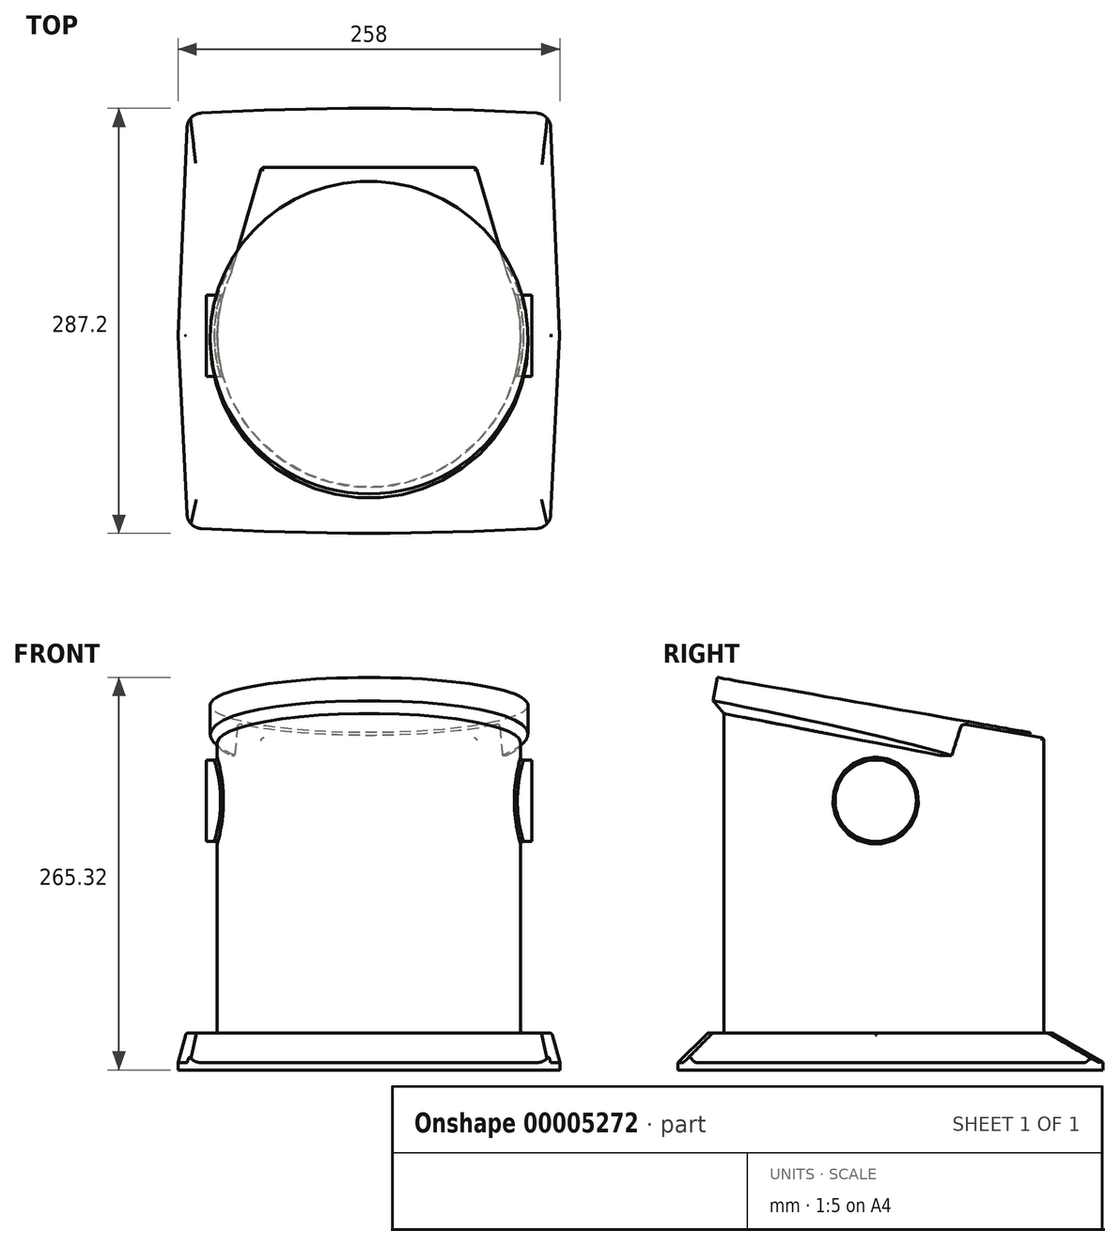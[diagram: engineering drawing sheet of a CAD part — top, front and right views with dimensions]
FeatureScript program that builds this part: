
annotation { "Feature Type Name" : "Feature", "Feature Type Description" : "" }
export const myFeature = defineFeature(function(context is Context, id is Id, definition is map)
    precondition{}
    {
        {
            var Q0;
            Q0=qCreatedBy(makeId("Top.planeOp"),FACE);
            var sketch = newSketch(context, id + "F0", { "sketchPlane" : qUnion([Q0])});
            skLineSegment(sketch, "E0", {"start": v(-129, 0) * mm, "end": v(-122.5, 149.86) * mm});
            skLineSegment(sketch, "E1", {"start": v(-122.5, 149.86) * mm, "end": v(122.5, 149.86) * mm, "construction": true});
            skLineSegment(sketch, "E2", {"start": v(122.5, 149.86) * mm, "end": v(129, 0) * mm});
            skLineSegment(sketch, "E3", {"start": v(129, 0) * mm, "end": v(122.5, -129.84) * mm});
            skLineSegment(sketch, "E4", {"start": v(122.5, -129.84) * mm, "end": v(-122.5, -129.84) * mm, "construction": true});
            skLineSegment(sketch, "E5", {"start": v(-122.5, -129.84) * mm, "end": v(-129, 0) * mm});
            skArc(sketch, "E6", {"start": v(122.5, 149.86) * mm, "mid": v(0, 153.61) * mm, "end": v(-122.5, 149.86) * mm});
            skArc(sketch, "E7", {"start": v(-122.5, -129.84) * mm, "mid": v(0, -133.6) * mm, "end": v(122.5, -129.84) * mm});
            skLineSegment(sketch, "E8", {"start": v(-129, 0) * mm, "end": v(129, 0) * mm, "construction": true});
            skPoint(sketch, "E9", {"position": v(0, 0) * mm});
            skPoint(sketch, "E10", {"position": v(0, 149.86) * mm});
            skPoint(sketch, "E11", {"position": v(0, -129.84) * mm});
            skSolve(sketch);
        }
        {
            var Q0;
            Q0=makeQuery(id+"F0.imprint","IMPRINT",FACE,{"disambiguationData":[TD([[makeQuery(id+"F0.imprint","IMPRINT",EDGE,{"derivedFrom":sQuery(id+"F0.wireOp",EDGE,"E0")}),-1.0]])]});
            extrude(context, id + "F1", {"entities" : qUnion([Q0]), "depth" : 25 * mm});
        }
        {
            var Q0;
            Q0=makeQuery(id+"F1.opExtrude","CAP_EDGE",EDGE,{"disambiguationData":[OSD([sQuery(id+"F0.wireOp",EDGE,"E0")])],"isStart":false});
            var Q1;
            Q1=makeQuery(id+"F1.opExtrude","CAP_EDGE",EDGE,{"disambiguationData":[OSD([sQuery(id+"F0.wireOp",EDGE,"E5")])],"isStart":false});
            var Q2;
            Q2=makeQuery(id+"F1.opExtrude","CAP_EDGE",EDGE,{"disambiguationData":[OSD([sQuery(id+"F0.wireOp",EDGE,"E3")])],"isStart":false});
            var Q3;
            Q3=makeQuery(id+"F1.opExtrude","CAP_EDGE",EDGE,{"disambiguationData":[OSD([sQuery(id+"F0.wireOp",EDGE,"E2")])],"isStart":false});
            chamfer(context, id + "F2", {"entities" : qUnion([Q0, Q1, Q2, Q3]), "chamferType" : ChamferType.OFFSET_ANGLE, "width" : 20 * mm, "oppositeDirection" : false, "angle" : 15 * degree, "tangentPropagation" : true});
        }
        {
            var Q0;
            Q0=makeQuery(id+"F1.opExtrude","CAP_EDGE",EDGE,{"disambiguationData":[OSD([sQuery(id+"F0.wireOp",EDGE,"E7")])],"isStart":false});
            chamfer(context, id + "F3", {"entities" : qUnion([Q0]), "chamferType" : ChamferType.OFFSET_ANGLE, "width" : 20 * mm, "oppositeDirection" : false, "angle" : 45 * degree, "tangentPropagation" : true});
        }
        {
            var Q0;
            Q0=makeQuery(id+"F1.opExtrude","CAP_EDGE",EDGE,{"disambiguationData":[OSD([sQuery(id+"F0.wireOp",EDGE,"E6")])],"isStart":false});
            chamfer(context, id + "F4", {"entities" : qUnion([Q0]), "chamferType" : ChamferType.OFFSET_ANGLE, "width" : 34 * mm, "oppositeDirection" : false, "angle" : 30 * degree, "tangentPropagation" : true});
        }
        {
            var Q0;
            Q0=makeQuery(id+"F1.opExtrude","CAP_FACE",FACE,{"disambiguationData":[OSD([sQuery(id+"F0.wireOp",EDGE,"E0"),sQuery(id+"F0.wireOp",EDGE,"E2"),sQuery(id+"F0.wireOp",EDGE,"E3"),sQuery(id+"F0.wireOp",EDGE,"E5"),sQuery(id+"F0.wireOp",EDGE,"E6"),sQuery(id+"F0.wireOp",EDGE,"E7")])],"isStart":false});
            var sketch = newSketch(context, id + "F5", { "sketchPlane" : qUnion([Q0])});
            skArc(sketch, "E12", {"start": v(-92.81, 43.5) * mm, "mid": v(0, -102.5) * mm, "end": v(92.81, 43.5) * mm});
            skLineSegment(sketch, "E13", {"start": v(-92.81, 43.5) * mm, "end": v(-72.5, 113.61) * mm});
            skLineSegment(sketch, "E14", {"start": v(-72.5, 113.61) * mm, "end": v(72.5, 113.61) * mm});
            skLineSegment(sketch, "E15", {"start": v(72.5, 113.61) * mm, "end": v(92.81, 43.5) * mm});
            skPoint(sketch, "E16", {"position": v(0, 113.61) * mm});
            skSolve(sketch);
        }
        {
            var Q0;
            Q0=makeQuery(id+"F5.imprint","IMPRINT",FACE,{"disambiguationData":[TD([[makeQuery(id+"F5.imprint","IMPRINT",EDGE,{"derivedFrom":sQuery(id+"F5.wireOp",EDGE,"E12")}),1.0]])]});
            extrude(context, id + "F6", {"entities" : qUnion([Q0]), "operationType" : NewBodyOperationType.ADD, "depth" : 240 * mm});
        }
        {
            var Q0;
            Q0=makeQuery(id+"F6.opExtrude","CAP_EDGE",EDGE,{"disambiguationData":[OSD([sQuery(id+"F5.wireOp",EDGE,"E14")])],"isStart":false});
            cPlane(context, id + "F7", {"entities" : qUnion([Q0]), "cplaneType" : CPlaneType.LINE_ANGLE, "offset" : 150 * mm, "angle" : 80 * degree, "width" : 150 * mm, "height" : 150 * mm});
        }
        {
            var Q0;
            Q0=qCreatedBy(id+"F7.planeOp",FACE);
            var sketch = newSketch(context, id + "F8", { "sketchPlane" : qUnion([Q0])});
            skCircle(sketch, "E17", {"center": v(0, -11.31) * mm, "radius": 170.12 * mm});
            skSolve(sketch);
        }
        {
            var Q0;
            Q0=makeQuery(id+"F8.imprint","IMPRINT",FACE,{"disambiguationData":[TD([[makeQuery(id+"F8.imprint","IMPRINT",EDGE,{"derivedFrom":sQuery(id+"F8.wireOp",EDGE,"E17")}),1.0]])]});
            extrude(context, id + "F9", {"entities" : qUnion([Q0]), "operationType" : NewBodyOperationType.REMOVE, "oppositeDirection" : true, "depth" : 40 * mm});
        }
        {
            var Q0;
            Q0=makeQuery(id+"F9.boolean.opBoolean","COPY",FACE,{"derivedFrom":makeQuery(id+"F9.opExtrude","CAP_FACE",FACE,{"disambiguationData":[OSD([sQuery(id+"F8.wireOp",EDGE,"E17")])],"isStart":false})});
            var sketch = newSketch(context, id + "F10", { "sketchPlane" : qUnion([Q0])});
            skCircle(sketch, "E18", {"center": v(0.1, -44.14) * mm, "radius": 102.33 * mm, "construction": true});
            skPoint(sketch, "E18.first.point", {"position": v(-100.45, -63.15) * mm});
            skPoint(sketch, "E18.second.point", {"position": v(21.64, -144.18) * mm});
            skPoint(sketch, "E18.third.point", {"position": v(102.35, -48.13) * mm});
            skCircle(sketch, "E19.0", {"center": v(0.1, -44.14) * mm, "radius": 107.33 * mm});
            skSolve(sketch);
        }
        {
            var Q0;
            Q0=qCreatedBy(makeId("Right.planeOp"),FACE);
            var sketch = newSketch(context, id + "F11", { "sketchPlane" : qUnion([Q0])});
            skCircle(sketch, "E20", {"center": v(0, 182) * mm, "radius": 27.5 * mm});
            skSolve(sketch);
        }
        {
            var Q0;
            Q0=makeQuery(id+"F11.imprint","IMPRINT",FACE,{"disambiguationData":[TD([[makeQuery(id+"F11.imprint","IMPRINT",EDGE,{"derivedFrom":sQuery(id+"F11.wireOp",EDGE,"E20")}),1.0]])]});
            extrude(context, id + "F12", {"entities" : qUnion([Q0]), "operationType" : NewBodyOperationType.ADD, "depth" : 110 * mm});
        }
        {
            var Q0;
            Q0=makeQuery(id+"F11.imprint","IMPRINT",FACE,{"disambiguationData":[TD([[makeQuery(id+"F11.imprint","IMPRINT",EDGE,{"derivedFrom":sQuery(id+"F11.wireOp",EDGE,"E20")}),1.0]])]});
            extrude(context, id + "F13", {"entities" : qUnion([Q0]), "operationType" : NewBodyOperationType.ADD, "oppositeDirection" : true, "depth" : 110 * mm});
        }
        {
            var Q0;
            Q0=makeQuery(id+"F1.opExtrude","CAP_FACE",FACE,{"disambiguationData":[OSD([sQuery(id+"F0.wireOp",EDGE,"E0"),sQuery(id+"F0.wireOp",EDGE,"E2"),sQuery(id+"F0.wireOp",EDGE,"E3"),sQuery(id+"F0.wireOp",EDGE,"E5"),sQuery(id+"F0.wireOp",EDGE,"E6"),sQuery(id+"F0.wireOp",EDGE,"E7")])],"isStart":false});
            var Q1;
            Q1=makeQuery(id+"F6.opExtrude","SWEPT_FACE",FACE,{"disambiguationData":[OSD([sQuery(id+"F5.wireOp",EDGE,"E14")])]});
            var Q2;
            Q2=makeQuery(id+"F6.opExtrude","SWEPT_FACE",FACE,{"disambiguationData":[OSD([sQuery(id+"F5.wireOp",EDGE,"E13")])]});
            var Q3;
            Q3=makeQuery(id+"F6.opExtrude","SWEPT_FACE",FACE,{"disambiguationData":[OSD([sQuery(id+"F5.wireOp",EDGE,"E12")])]});
            var Q4;
            Q4=makeQuery(id+"F9.boolean.opBoolean","COPY",FACE,{"derivedFrom":makeQuery(id+"F9.opExtrude","CAP_FACE",FACE,{"disambiguationData":[OSD([sQuery(id+"F8.wireOp",EDGE,"E17")])],"isStart":false})});
            var Q5;
            Q5=makeQuery(id+"F6.opExtrude","SWEPT_FACE",FACE,{"disambiguationData":[OSD([sQuery(id+"F5.wireOp",EDGE,"E15")])]});
            var Q6;
            Q6=makeQuery(id+"F3.opChamfer","BLEND_EDGE",EDGE,{"blendedFrom":[makeQuery(id+"F1.opExtrude","CAP_EDGE",EDGE,{"disambiguationData":[OSD([sQuery(id+"F0.wireOp",EDGE,"E7")])],"isStart":false}),makeQuery(id+"F2.opChamfer","BLEND_FACE",FACE,{"disambiguationData":[OSD([sQuery(id+"F0.wireOp",EDGE,"E5")])]})],"blendedInto":[makeQuery(id+"F2.opChamfer","BLEND_FACE",FACE,{"disambiguationData":[OSD([sQuery(id+"F0.wireOp",EDGE,"E5")])]})]});
            var Q7;
            Q7=makeQuery(id+"F3.opChamfer","BLEND_EDGE",EDGE,{"blendedFrom":[makeQuery(id+"F1.opExtrude","CAP_EDGE",EDGE,{"disambiguationData":[OSD([sQuery(id+"F0.wireOp",EDGE,"E7")])],"isStart":false}),makeQuery(id+"F2.opChamfer","BLEND_FACE",FACE,{"disambiguationData":[OSD([sQuery(id+"F0.wireOp",EDGE,"E3")])]})],"blendedInto":[makeQuery(id+"F2.opChamfer","BLEND_FACE",FACE,{"disambiguationData":[OSD([sQuery(id+"F0.wireOp",EDGE,"E3")])]})]});
            var Q8;
            Q8=makeQuery(id+"F4.opChamfer","BLEND_EDGE",EDGE,{"blendedFrom":[makeQuery(id+"F1.opExtrude","CAP_EDGE",EDGE,{"disambiguationData":[OSD([sQuery(id+"F0.wireOp",EDGE,"E6")])],"isStart":false}),makeQuery(id+"F2.opChamfer","BLEND_FACE",FACE,{"disambiguationData":[OSD([sQuery(id+"F0.wireOp",EDGE,"E2")])]})],"blendedInto":[makeQuery(id+"F2.opChamfer","BLEND_FACE",FACE,{"disambiguationData":[OSD([sQuery(id+"F0.wireOp",EDGE,"E2")])]})]});
            var Q9;
            Q9=makeQuery(id+"F4.opChamfer","BLEND_EDGE",EDGE,{"blendedFrom":[makeQuery(id+"F1.opExtrude","CAP_EDGE",EDGE,{"disambiguationData":[OSD([sQuery(id+"F0.wireOp",EDGE,"E6")])],"isStart":false}),makeQuery(id+"F2.opChamfer","BLEND_FACE",FACE,{"disambiguationData":[OSD([sQuery(id+"F0.wireOp",EDGE,"E0")])]})],"blendedInto":[makeQuery(id+"F2.opChamfer","BLEND_FACE",FACE,{"disambiguationData":[OSD([sQuery(id+"F0.wireOp",EDGE,"E0")])]})]});
            var Q10;
            Q10=makeQuery(id+"F6.opExtrude","SWEPT_EDGE",EDGE,{"disambiguationData":[OSD([sQuery(id+"F5.wireOp",EDGE,"E12"),sQuery(id+"F5.wireOp",EDGE,"E15")])]});
            var Q11;
            Q11=makeQuery(id+"F2.opChamfer","BLEND_EDGE",EDGE,{"blendedFrom":[makeQuery(id+"F1.opExtrude","CAP_EDGE",EDGE,{"disambiguationData":[OSD([sQuery(id+"F0.wireOp",EDGE,"E2")])],"isStart":false}),makeQuery(id+"F1.opExtrude","CAP_EDGE",EDGE,{"disambiguationData":[OSD([sQuery(id+"F0.wireOp",EDGE,"E3")])],"isStart":false})],"blendedInto":[]});
            var Q12;
            Q12=makeQuery(id+"F1.opExtrude","SWEPT_EDGE",EDGE,{"disambiguationData":[OSD([sQuery(id+"F0.wireOp",EDGE,"E2"),sQuery(id+"F0.wireOp",EDGE,"E3")])]});
            var Q13;
            Q13=makeQuery(id+"F6.opExtrude","SWEPT_EDGE",EDGE,{"disambiguationData":[OSD([sQuery(id+"F5.wireOp",EDGE,"E12"),sQuery(id+"F5.wireOp",EDGE,"E13")])]});
            var Q14;
            Q14=makeQuery(id+"F2.opChamfer","BLEND_EDGE",EDGE,{"blendedFrom":[makeQuery(id+"F1.opExtrude","CAP_EDGE",EDGE,{"disambiguationData":[OSD([sQuery(id+"F0.wireOp",EDGE,"E0")])],"isStart":false}),makeQuery(id+"F1.opExtrude","CAP_EDGE",EDGE,{"disambiguationData":[OSD([sQuery(id+"F0.wireOp",EDGE,"E5")])],"isStart":false})],"blendedInto":[]});
            var Q15;
            Q15=makeQuery(id+"F1.opExtrude","SWEPT_EDGE",EDGE,{"disambiguationData":[OSD([sQuery(id+"F0.wireOp",EDGE,"E0"),sQuery(id+"F0.wireOp",EDGE,"E5")])]});
            fillet(context, id + "F14", {"entities" : qUnion([Q0, Q1, Q2, Q3, Q4, Q5, Q6, Q7, Q8, Q9, Q10, Q11, Q12, Q13, Q14, Q15]), "radius" : 2 * mm, "tangentPropagation" : true, "allowEdgeOverflow" : false});
        }
        {
            var Q0;
            Q0=makeQuery(id+"F1.opExtrude","SWEPT_EDGE",EDGE,{"disambiguationData":[OSD([sQuery(id+"F0.wireOp",EDGE,"E3"),sQuery(id+"F0.wireOp",EDGE,"E7")])]});
            var Q1;
            Q1=makeQuery(id+"F1.opExtrude","SWEPT_EDGE",EDGE,{"disambiguationData":[OSD([sQuery(id+"F0.wireOp",EDGE,"E2"),sQuery(id+"F0.wireOp",EDGE,"E6")])]});
            var Q2;
            Q2=makeQuery(id+"F1.opExtrude","SWEPT_EDGE",EDGE,{"disambiguationData":[OSD([sQuery(id+"F0.wireOp",EDGE,"E0"),sQuery(id+"F0.wireOp",EDGE,"E6")])]});
            var Q3;
            Q3=makeQuery(id+"F1.opExtrude","SWEPT_EDGE",EDGE,{"disambiguationData":[OSD([sQuery(id+"F0.wireOp",EDGE,"E5"),sQuery(id+"F0.wireOp",EDGE,"E7")])]});
            fillet(context, id + "F15", {"entities" : qUnion([Q0, Q1, Q2, Q3]), "radius" : 10 * mm, "tangentPropagation" : true, "allowEdgeOverflow" : false});
        }
        {
            var Q0;
            {var subQ0=makeQuery(id+"F9.opExtrude","CAP_FACE",FACE,{"disambiguationData":[OSD([sQuery(id+"F8.wireOp",EDGE,"E17")])],"isStart":false});var subQ4=makeQuery(id+"F9.boolean.opBoolean","INTERSECT",EDGE,{"derivedFrom":[makeQuery(id+"F6.opExtrude","SWEPT_FACE",FACE,{"disambiguationData":[OSD([sQuery(id+"F5.wireOp",EDGE,"E12")])]}),subQ0]});var subQ9=makeQuery(id+"F10.imprint","IMPRINT",EDGE,{"derivedFrom":subQ4});Q0=qUnion([makeQuery(id+"F10.imprint","IMPRINT",FACE,{"disambiguationData":[TD([[subQ9,-1.0]])]}),makeQuery(id+"F10.imprint","IMPRINT",FACE,{"disambiguationData":[TD([[subQ9,1.0]])]})]);}
            extrude(context, id + "F16", {"entities" : qUnion([Q0]), "operationType" : NewBodyOperationType.ADD, "depth" : 2 * mm});
        }
        {
            var Q0;
            {var subQ0=makeQuery(id+"F9.opExtrude","CAP_FACE",FACE,{"disambiguationData":[OSD([sQuery(id+"F8.wireOp",EDGE,"E17")])],"isStart":false});var subQ4=makeQuery(id+"F9.boolean.opBoolean","INTERSECT",EDGE,{"derivedFrom":[makeQuery(id+"F6.opExtrude","SWEPT_FACE",FACE,{"disambiguationData":[OSD([sQuery(id+"F5.wireOp",EDGE,"E12")])]}),subQ0]});var subQ9=makeQuery(id+"F10.imprint","IMPRINT",EDGE,{"derivedFrom":subQ4});Q0=qUnion([makeQuery(id+"F10.imprint","IMPRINT",FACE,{"disambiguationData":[TD([[subQ9,-1.0]])]}),makeQuery(id+"F10.imprint","IMPRINT",FACE,{"disambiguationData":[TD([[subQ9,1.0]])]})]);}
            extrude(context, id + "F17", {"entities" : qUnion([Q0]), "operationType" : NewBodyOperationType.ADD, "oppositeDirection" : true, "depth" : 13 * mm});
        }
        {
            var Q0;
            Q0=makeQuery(id+"F17.boolean.opBoolean","INTERSECT",EDGE,{"derivedFrom":[makeQuery(id+"F6.opExtrude","SWEPT_FACE",FACE,{"disambiguationData":[OSD([sQuery(id+"F5.wireOp",EDGE,"E12")])]}),makeQuery(id+"F17.opExtrude","CAP_FACE",FACE,{"disambiguationData":[OSD([sQuery(id+"F10.wireOp",EDGE,"E19.0")])],"isStart":false})]});
            chamfer(context, id + "F18", {"entities" : qUnion([Q0]), "width" : 10 * mm});
        }
    });
